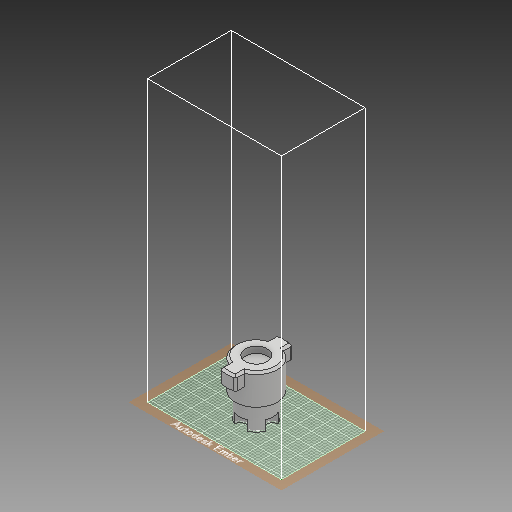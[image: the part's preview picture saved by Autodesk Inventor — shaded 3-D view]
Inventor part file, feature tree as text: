
AUTODESK INVENTOR PART (.ipt)
format: ipt  version: 2018 (Build 220112000, 112)  size: 369,152 bytes
history: native  units: mm
features: extrude x8, sketch x8, other x1, chamfer x1, fillet x1, pattern_circular x1, projected_geometry x1
ambient origin geometry x8: Origin, YZ Plane, XZ Plane, XY Plane, X Axis, Y Axis, Z Axis, Center Point
bodies: Body1 (feature_tree)
feature tree (21):
  other  "ソリッド1"
  extrude  "押し出し1"  Depth=20.0mm
  extrude  "押し出し2"  Depth=6.5mm TaperAngle=0.0deg
  chamfer  "面取り1"  Distance=14.0mm
  fillet  "フィレット1"  Radius=7.5mm
  extrude  "押し出し4"  Depth=6.5mm TaperAngle=0.0deg
  extrude  "押し出し5"  Depth=1.0mm TaperAngle=45.0deg
  extrude  "押し出し6"  Depth=1.0mm
  pattern_circular  "円形状パターン1"  [2 undecoded]
  extrude  "押し出し7"  Depth=19.0mm TaperAngle=0.0deg
  extrude  "押し出し8"  Depth=10.5mm
  extrude  "押し出し9"  Depth=3.0mm TaperAngle=0.0deg
  sketch  "スケッチ1"
  sketch  "スケッチ2"
  sketch  "スケッチ4"
  sketch  "スケッチ5"
  sketch  "スケッチ6"
  sketch  "スケッチ7"
  sketch  "スケッチ8"
  projected_geometry  "投影ループ1"
  sketch  "スケッチ9"
note: 2 required parameter values undecoded (feature->parameter linkage not recoverable at this tier; creation-order binding heuristic only, values carry confidence <= 0.55)
